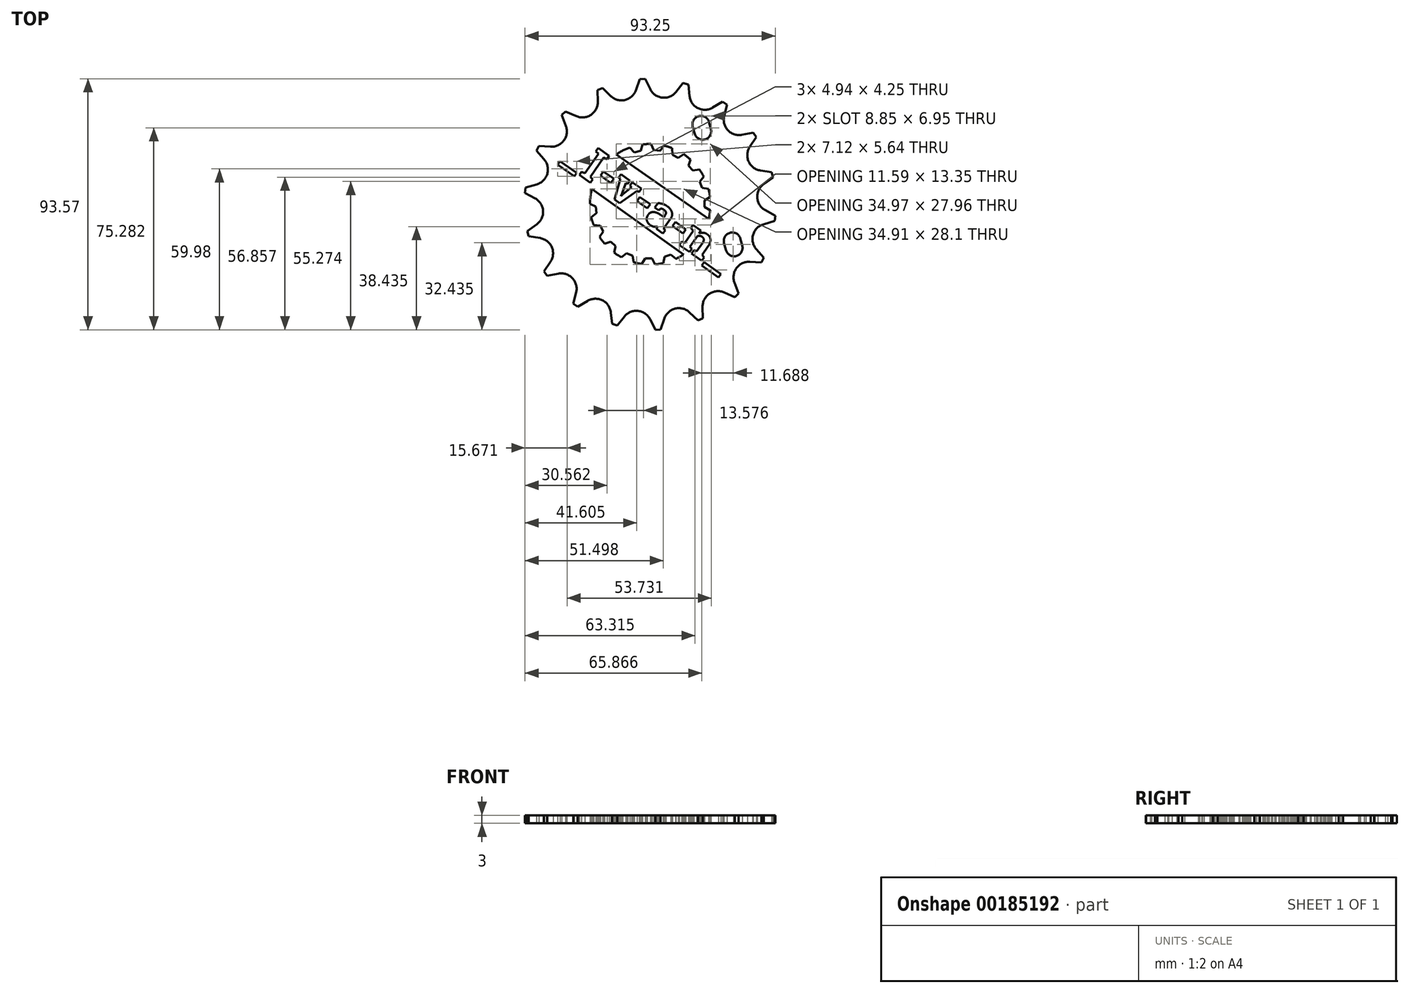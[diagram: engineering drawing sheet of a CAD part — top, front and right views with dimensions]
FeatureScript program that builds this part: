
annotation { "Feature Type Name" : "Feature", "Feature Type Description" : "" }
export const myFeature = defineFeature(function(context is Context, id is Id, definition is map)
    precondition{}
    {
        {
            var Q0;
            Q0=qCreatedBy(makeId("Top.planeOp"),FACE);
            var sketch = newSketch(context, id + "F0", { "sketchPlane" : qUnion([Q0])});
            skText(sketch, "E0", { "text": "_I-v-a-n_", "fontName": "RobotoSlab-Bold.ttf"});
            skCircle(sketch, "E1", {"center": v(-42.84, 44.1) * mm, "radius": 40 * mm});
            skLineSegment(sketch, "E2", {"start": v(-49.19, 83.6) * mm, "end": v(-46.73, 90.76) * mm, "construction": true});
            skLineSegment(sketch, "E3", {"start": v(-46.73, 90.76) * mm, "end": v(-44.73, 90.89) * mm});
            skLineSegment(sketch, "E4", {"start": v(-44.73, 90.89) * mm, "end": v(-41.4, 84.08) * mm, "construction": true});
            skLineSegment(sketch, "E5", {"start": v(-41.4, 84.08) * mm, "end": v(-49.19, 83.6) * mm, "construction": true});
            skArc(sketch, "E6", {"start": v(-42.85, 87.03) * mm, "mid": v(-38.34, 83.85) * mm, "end": v(-33.23, 85.94) * mm});
            skLineSegment(sketch, "E7", {"start": v(-42.85, 87.03) * mm, "end": v(-44.73, 90.89) * mm});
            skLineSegment(sketch, "E8", {"start": v(-48.12, 86.7) * mm, "end": v(-46.73, 90.76) * mm});
            skLineSegment(sketch, "E9.1.0", {"start": v(-55.16, 82.16) * mm, "end": v(-62.31, 79.04) * mm, "construction": true});
            skLineSegment(sketch, "E9.1.2", {"start": v(-62.31, 79.04) * mm, "end": v(-62.45, 86.62) * mm, "construction": true});
            skArc(sketch, "E9.1.3", {"start": v(-57.53, 84.44) * mm, "mid": v(-52.2, 83) * mm, "end": v(-48.12, 86.7) * mm});
            skLineSegment(sketch, "E9.1.4", {"start": v(-60.62, 87.42) * mm, "end": v(-55.16, 82.16) * mm, "construction": true});
            skLineSegment(sketch, "E9.1.5", {"start": v(-62.37, 82.33) * mm, "end": v(-62.45, 86.62) * mm});
            skLineSegment(sketch, "E9.1.6", {"start": v(-57.53, 84.44) * mm, "end": v(-60.62, 87.42) * mm});
            skLineSegment(sketch, "E9.1.7", {"start": v(-62.45, 86.62) * mm, "end": v(-60.62, 87.42) * mm});
            skLineSegment(sketch, "E9.2.0", {"start": v(-67.43, 75.65) * mm, "end": v(-73.09, 70.27) * mm, "construction": true});
            skLineSegment(sketch, "E9.2.2", {"start": v(-73.09, 70.27) * mm, "end": v(-75.8, 77.34) * mm, "construction": true});
            skArc(sketch, "E9.2.3", {"start": v(-70.44, 76.98) * mm, "mid": v(-64.94, 77.44) * mm, "end": v(-62.37, 82.33) * mm});
            skLineSegment(sketch, "E9.2.4", {"start": v(-74.36, 78.72) * mm, "end": v(-67.43, 75.65) * mm, "construction": true});
            skLineSegment(sketch, "E9.2.5", {"start": v(-74.27, 73.34) * mm, "end": v(-75.8, 77.34) * mm});
            skLineSegment(sketch, "E9.2.6", {"start": v(-70.44, 76.98) * mm, "end": v(-74.36, 78.72) * mm});
            skLineSegment(sketch, "E9.2.7", {"start": v(-75.8, 77.34) * mm, "end": v(-74.36, 78.72) * mm});
            skLineSegment(sketch, "E9.3.0", {"start": v(-76.74, 65.33) * mm, "end": v(-80.21, 58.35) * mm, "construction": true});
            skLineSegment(sketch, "E9.3.2", {"start": v(-80.21, 58.35) * mm, "end": v(-85.19, 64.06) * mm, "construction": true});
            skArc(sketch, "E9.3.3", {"start": v(-80.02, 65.56) * mm, "mid": v(-75, 67.87) * mm, "end": v(-74.27, 73.34) * mm});
            skLineSegment(sketch, "E9.3.4", {"start": v(-84.3, 65.85) * mm, "end": v(-76.74, 65.33) * mm, "construction": true});
            skLineSegment(sketch, "E9.3.5", {"start": v(-82.37, 60.83) * mm, "end": v(-85.19, 64.06) * mm});
            skLineSegment(sketch, "E9.3.6", {"start": v(-80.02, 65.56) * mm, "end": v(-84.3, 65.85) * mm});
            skLineSegment(sketch, "E9.3.7", {"start": v(-85.19, 64.06) * mm, "end": v(-84.3, 65.85) * mm});
            skLineSegment(sketch, "E9.4.0", {"start": v(-81.95, 52.45) * mm, "end": v(-82.83, 44.7) * mm, "construction": true});
            skLineSegment(sketch, "E9.4.2", {"start": v(-82.83, 44.7) * mm, "end": v(-89.46, 48.37) * mm, "construction": true});
            skArc(sketch, "E9.4.3", {"start": v(-85.11, 51.55) * mm, "mid": v(-81.2, 55.43) * mm, "end": v(-82.37, 60.83) * mm});
            skLineSegment(sketch, "E9.4.4", {"start": v(-89.24, 50.36) * mm, "end": v(-81.95, 52.45) * mm, "construction": true});
            skLineSegment(sketch, "E9.4.5", {"start": v(-85.7, 46.3) * mm, "end": v(-89.46, 48.37) * mm});
            skLineSegment(sketch, "E9.4.6", {"start": v(-85.11, 51.55) * mm, "end": v(-89.24, 50.36) * mm});
            skLineSegment(sketch, "E9.4.7", {"start": v(-89.46, 48.37) * mm, "end": v(-89.24, 50.36) * mm});
            skLineSegment(sketch, "E9.5.0", {"start": v(-82.45, 38.57) * mm, "end": v(-80.62, 30.99) * mm, "construction": true});
            skLineSegment(sketch, "E9.5.2", {"start": v(-80.62, 30.99) * mm, "end": v(-88.1, 32.17) * mm, "construction": true});
            skArc(sketch, "E9.5.3", {"start": v(-85.1, 36.64) * mm, "mid": v(-82.76, 41.63) * mm, "end": v(-85.7, 46.3) * mm});
            skLineSegment(sketch, "E9.5.4", {"start": v(-88.58, 34.11) * mm, "end": v(-82.45, 38.57) * mm, "construction": true});
            skLineSegment(sketch, "E9.5.5", {"start": v(-83.87, 31.5) * mm, "end": v(-88.1, 32.17) * mm});
            skLineSegment(sketch, "E9.5.6", {"start": v(-85.1, 36.64) * mm, "end": v(-88.58, 34.11) * mm});
            skLineSegment(sketch, "E9.5.7", {"start": v(-88.1, 32.17) * mm, "end": v(-88.58, 34.11) * mm});
            skLineSegment(sketch, "E9.6.0", {"start": v(-78.17, 25.36) * mm, "end": v(-73.86, 18.86) * mm, "construction": true});
            skLineSegment(sketch, "E9.6.2", {"start": v(-73.86, 18.86) * mm, "end": v(-81.3, 17.4) * mm, "construction": true});
            skArc(sketch, "E9.6.3", {"start": v(-80, 22.63) * mm, "mid": v(-79.5, 28.13) * mm, "end": v(-83.87, 31.5) * mm});
            skLineSegment(sketch, "E9.6.4", {"start": v(-82.4, 19.07) * mm, "end": v(-78.17, 25.36) * mm, "construction": true});
            skLineSegment(sketch, "E9.6.5", {"start": v(-77.09, 18.23) * mm, "end": v(-81.3, 17.4) * mm});
            skLineSegment(sketch, "E9.6.6", {"start": v(-80, 22.63) * mm, "end": v(-82.4, 19.07) * mm});
            skLineSegment(sketch, "E9.6.7", {"start": v(-81.3, 17.4) * mm, "end": v(-82.4, 19.07) * mm});
            skLineSegment(sketch, "E9.7.0", {"start": v(-69.63, 14.4) * mm, "end": v(-63.35, 9.77) * mm, "construction": true});
            skLineSegment(sketch, "E9.7.2", {"start": v(-63.35, 9.77) * mm, "end": v(-69.85, 5.86) * mm, "construction": true});
            skArc(sketch, "E9.7.3", {"start": v(-70.42, 11.21) * mm, "mid": v(-71.83, 16.55) * mm, "end": v(-77.09, 18.23) * mm});
            skLineSegment(sketch, "E9.7.4", {"start": v(-71.45, 7.05) * mm, "end": v(-69.63, 14.4) * mm, "construction": true});
            skLineSegment(sketch, "E9.7.5", {"start": v(-66.17, 8.07) * mm, "end": v(-69.85, 5.86) * mm});
            skLineSegment(sketch, "E9.7.6", {"start": v(-70.42, 11.21) * mm, "end": v(-71.45, 7.05) * mm});
            skLineSegment(sketch, "E9.7.7", {"start": v(-69.85, 5.86) * mm, "end": v(-71.45, 7.05) * mm});
            skLineSegment(sketch, "E9.8.0", {"start": v(-57.85, 7.03) * mm, "end": v(-50.37, 4.82) * mm, "construction": true});
            skLineSegment(sketch, "E9.8.2", {"start": v(-50.37, 4.82) * mm, "end": v(-55.14, -1.07) * mm, "construction": true});
            skArc(sketch, "E9.8.3", {"start": v(-57.5, 3.76) * mm, "mid": v(-60.66, 8.3) * mm, "end": v(-66.17, 8.07) * mm});
            skLineSegment(sketch, "E9.8.4", {"start": v(-57.05, -0.5) * mm, "end": v(-57.85, 7.03) * mm, "construction": true});
            skLineSegment(sketch, "E9.8.5", {"start": v(-52.44, 2.26) * mm, "end": v(-55.14, -1.07) * mm});
            skLineSegment(sketch, "E9.8.6", {"start": v(-57.5, 3.76) * mm, "end": v(-57.05, -0.5) * mm});
            skLineSegment(sketch, "E9.8.7", {"start": v(-55.14, -1.07) * mm, "end": v(-57.05, -0.5) * mm});
            skLineSegment(sketch, "E9.9.0", {"start": v(-44.27, 4.13) * mm, "end": v(-36.48, 4.61) * mm, "construction": true});
            skLineSegment(sketch, "E9.9.2", {"start": v(-36.48, 4.61) * mm, "end": v(-38.94, -2.55) * mm, "construction": true});
            skArc(sketch, "E9.9.3", {"start": v(-42.82, 1.18) * mm, "mid": v(-47.33, 4.36) * mm, "end": v(-52.44, 2.26) * mm});
            skLineSegment(sketch, "E9.9.4", {"start": v(-40.94, -2.68) * mm, "end": v(-44.27, 4.13) * mm, "construction": true});
            skLineSegment(sketch, "E9.9.5", {"start": v(-37.55, 1.5) * mm, "end": v(-38.94, -2.55) * mm});
            skLineSegment(sketch, "E9.9.6", {"start": v(-42.82, 1.18) * mm, "end": v(-40.94, -2.68) * mm});
            skLineSegment(sketch, "E9.9.7", {"start": v(-38.94, -2.55) * mm, "end": v(-40.94, -2.68) * mm});
            skLineSegment(sketch, "E9.10.0", {"start": v(-30.5, 6.05) * mm, "end": v(-23.36, 9.17) * mm, "construction": true});
            skLineSegment(sketch, "E9.10.2", {"start": v(-23.36, 9.17) * mm, "end": v(-23.22, 1.6) * mm, "construction": true});
            skArc(sketch, "E9.10.3", {"start": v(-28.14, 3.77) * mm, "mid": v(-33.47, 5.22) * mm, "end": v(-37.55, 1.5) * mm});
            skLineSegment(sketch, "E9.10.4", {"start": v(-25.05, 0.8) * mm, "end": v(-30.5, 6.05) * mm, "construction": true});
            skLineSegment(sketch, "E9.10.5", {"start": v(-23.3, 5.88) * mm, "end": v(-23.22, 1.6) * mm});
            skLineSegment(sketch, "E9.10.6", {"start": v(-28.14, 3.77) * mm, "end": v(-25.05, 0.8) * mm});
            skLineSegment(sketch, "E9.10.7", {"start": v(-23.22, 1.6) * mm, "end": v(-25.05, 0.8) * mm});
            skLineSegment(sketch, "E9.11.0", {"start": v(-18.24, 12.56) * mm, "end": v(-12.58, 17.93) * mm, "construction": true});
            skLineSegment(sketch, "E9.11.2", {"start": v(-12.58, 17.93) * mm, "end": v(-9.86, 10.86) * mm, "construction": true});
            skArc(sketch, "E9.11.3", {"start": v(-15.23, 11.23) * mm, "mid": v(-20.73, 10.77) * mm, "end": v(-23.3, 5.88) * mm});
            skLineSegment(sketch, "E9.11.4", {"start": v(-11.31, 9.49) * mm, "end": v(-18.24, 12.56) * mm, "construction": true});
            skLineSegment(sketch, "E9.11.5", {"start": v(-11.4, 14.87) * mm, "end": v(-9.86, 10.86) * mm});
            skLineSegment(sketch, "E9.11.6", {"start": v(-15.23, 11.23) * mm, "end": v(-11.31, 9.49) * mm});
            skLineSegment(sketch, "E9.11.7", {"start": v(-9.86, 10.86) * mm, "end": v(-11.31, 9.49) * mm});
            skLineSegment(sketch, "E9.12.0", {"start": v(-8.93, 22.88) * mm, "end": v(-5.46, 29.86) * mm, "construction": true});
            skLineSegment(sketch, "E9.12.2", {"start": v(-5.46, 29.86) * mm, "end": v(-0.48, 24.15) * mm, "construction": true});
            skArc(sketch, "E9.12.3", {"start": v(-5.65, 22.65) * mm, "mid": v(-10.66, 20.34) * mm, "end": v(-11.4, 14.87) * mm});
            skLineSegment(sketch, "E9.12.4", {"start": v(-1.37, 22.35) * mm, "end": v(-8.93, 22.88) * mm, "construction": true});
            skLineSegment(sketch, "E9.12.5", {"start": v(-3.3, 27.38) * mm, "end": v(-0.48, 24.15) * mm});
            skLineSegment(sketch, "E9.12.6", {"start": v(-5.65, 22.65) * mm, "end": v(-1.37, 22.35) * mm});
            skLineSegment(sketch, "E9.12.7", {"start": v(-0.48, 24.15) * mm, "end": v(-1.37, 22.35) * mm});
            skLineSegment(sketch, "E9.13.0", {"start": v(-3.72, 35.75) * mm, "end": v(-2.84, 43.5) * mm, "construction": true});
            skLineSegment(sketch, "E9.13.2", {"start": v(-2.84, 43.5) * mm, "end": v(3.79, 39.83) * mm, "construction": true});
            skArc(sketch, "E9.13.3", {"start": v(-0.56, 36.66) * mm, "mid": v(-4.47, 32.77) * mm, "end": v(-3.3, 27.38) * mm});
            skLineSegment(sketch, "E9.13.4", {"start": v(3.56, 37.85) * mm, "end": v(-3.72, 35.75) * mm, "construction": true});
            skLineSegment(sketch, "E9.13.5", {"start": v(0.04, 41.91) * mm, "end": v(3.79, 39.83) * mm});
            skLineSegment(sketch, "E9.13.6", {"start": v(-0.56, 36.66) * mm, "end": v(3.56, 37.85) * mm});
            skLineSegment(sketch, "E9.13.7", {"start": v(3.79, 39.83) * mm, "end": v(3.56, 37.85) * mm});
            skLineSegment(sketch, "E9.14.0", {"start": v(-3.22, 49.64) * mm, "end": v(-5.05, 57.22) * mm, "construction": true});
            skLineSegment(sketch, "E9.14.2", {"start": v(-5.05, 57.22) * mm, "end": v(2.44, 56.04) * mm, "construction": true});
            skArc(sketch, "E9.14.3", {"start": v(-0.56, 51.57) * mm, "mid": v(-2.91, 46.58) * mm, "end": v(0.04, 41.91) * mm});
            skLineSegment(sketch, "E9.14.4", {"start": v(2.9, 54.1) * mm, "end": v(-3.22, 49.64) * mm, "construction": true});
            skLineSegment(sketch, "E9.14.5", {"start": v(-1.8, 56.7) * mm, "end": v(2.44, 56.04) * mm});
            skLineSegment(sketch, "E9.14.6", {"start": v(-0.56, 51.57) * mm, "end": v(2.9, 54.1) * mm});
            skLineSegment(sketch, "E9.14.7", {"start": v(2.44, 56.04) * mm, "end": v(2.9, 54.1) * mm});
            skLineSegment(sketch, "E9.15.0", {"start": v(-7.5, 62.85) * mm, "end": v(-11.81, 69.35) * mm, "construction": true});
            skLineSegment(sketch, "E9.15.2", {"start": v(-11.81, 69.35) * mm, "end": v(-4.37, 70.8) * mm, "construction": true});
            skArc(sketch, "E9.15.3", {"start": v(-5.66, 65.58) * mm, "mid": v(-6.17, 60.08) * mm, "end": v(-1.8, 56.7) * mm});
            skLineSegment(sketch, "E9.15.4", {"start": v(-3.27, 69.14) * mm, "end": v(-7.5, 62.85) * mm, "construction": true});
            skLineSegment(sketch, "E9.15.5", {"start": v(-8.58, 69.98) * mm, "end": v(-4.37, 70.8) * mm});
            skLineSegment(sketch, "E9.15.6", {"start": v(-5.66, 65.58) * mm, "end": v(-3.27, 69.14) * mm});
            skLineSegment(sketch, "E9.15.7", {"start": v(-4.37, 70.8) * mm, "end": v(-3.27, 69.14) * mm});
            skLineSegment(sketch, "E9.16.0", {"start": v(-16.04, 73.8) * mm, "end": v(-22.32, 78.44) * mm, "construction": true});
            skLineSegment(sketch, "E9.16.2", {"start": v(-22.32, 78.44) * mm, "end": v(-15.83, 82.35) * mm, "construction": true});
            skArc(sketch, "E9.16.3", {"start": v(-15.25, 77) * mm, "mid": v(-13.84, 71.66) * mm, "end": v(-8.58, 69.98) * mm});
            skLineSegment(sketch, "E9.16.4", {"start": v(-14.22, 81.16) * mm, "end": v(-16.04, 73.8) * mm, "construction": true});
            skLineSegment(sketch, "E9.16.5", {"start": v(-19.5, 80.14) * mm, "end": v(-15.83, 82.35) * mm});
            skLineSegment(sketch, "E9.16.6", {"start": v(-15.25, 77) * mm, "end": v(-14.22, 81.16) * mm});
            skLineSegment(sketch, "E9.16.7", {"start": v(-15.83, 82.35) * mm, "end": v(-14.22, 81.16) * mm});
            skLineSegment(sketch, "E9.17.0", {"start": v(-27.82, 81.18) * mm, "end": v(-35.3, 83.39) * mm, "construction": true});
            skLineSegment(sketch, "E9.17.2", {"start": v(-35.3, 83.39) * mm, "end": v(-30.53, 89.28) * mm, "construction": true});
            skArc(sketch, "E9.17.3", {"start": v(-28.16, 84.45) * mm, "mid": v(-25.02, 79.92) * mm, "end": v(-19.5, 80.14) * mm});
            skLineSegment(sketch, "E9.17.4", {"start": v(-28.62, 88.71) * mm, "end": v(-27.82, 81.18) * mm, "construction": true});
            skLineSegment(sketch, "E9.17.5", {"start": v(-33.23, 85.94) * mm, "end": v(-30.53, 89.28) * mm});
            skLineSegment(sketch, "E9.17.6", {"start": v(-28.16, 84.45) * mm, "end": v(-28.62, 88.71) * mm});
            skLineSegment(sketch, "E9.17.7", {"start": v(-30.53, 89.28) * mm, "end": v(-28.62, 88.71) * mm});
            skLineSegment(sketch, "E10", {"start": v(-102.27, 86.15) * mm, "end": v(16.6, 2.06) * mm, "construction": true});
            skLineSegment(sketch, "E11", {"start": v(-55.45, 62.7) * mm, "end": v(-21.04, 38.61) * mm});
            skArc(sketch, "E12", {"start": v(-55.45, 62.7) * mm, "mid": v(-29.95, 62.51) * mm, "end": v(-21.04, 38.61) * mm, "construction": true});
            skLineSegment(sketch, "E13", {"start": v(-50.46, 65.24) * mm, "end": v(-48.76, 63.46) * mm});
            skLineSegment(sketch, "E14", {"start": v(-48.76, 63.46) * mm, "end": v(-46.37, 64.04) * mm});
            skLineSegment(sketch, "E15", {"start": v(-46.37, 64.04) * mm, "end": v(-45.67, 66.4) * mm});
            skLineSegment(sketch, "E16", {"start": v(-45.67, 66.4) * mm, "end": v(-50.46, 65.24) * mm, "construction": true});
            skLineSegment(sketch, "E17", {"start": v(-53.55, 88.57) * mm, "end": v(-42.84, 44.1) * mm, "construction": true});
            skPoint(sketch, "E18", {"position": v(-47.57, 63.75) * mm});
            skLineSegment(sketch, "E19.1.0", {"start": v(-42.53, 66.57) * mm, "end": v(-41.57, 64.3) * mm});
            skLineSegment(sketch, "E19.1.1", {"start": v(-41.57, 64.3) * mm, "end": v(-39.13, 64) * mm});
            skLineSegment(sketch, "E19.1.2", {"start": v(-39.13, 64) * mm, "end": v(-37.65, 65.97) * mm});
            skLineSegment(sketch, "E19.2.0", {"start": v(-34.65, 65.03) * mm, "end": v(-34.55, 62.57) * mm});
            skLineSegment(sketch, "E19.2.1", {"start": v(-34.55, 62.57) * mm, "end": v(-32.37, 61.43) * mm});
            skLineSegment(sketch, "E19.2.2", {"start": v(-32.37, 61.43) * mm, "end": v(-30.29, 62.75) * mm});
            skLineSegment(sketch, "E19.3.0", {"start": v(-27.8, 60.81) * mm, "end": v(-28.58, 58.48) * mm});
            skLineSegment(sketch, "E19.3.1", {"start": v(-28.58, 58.48) * mm, "end": v(-26.94, 56.64) * mm});
            skLineSegment(sketch, "E19.3.2", {"start": v(-26.94, 56.64) * mm, "end": v(-24.53, 57.14) * mm});
            skLineSegment(sketch, "E19.4.0", {"start": v(-22.89, 54.46) * mm, "end": v(-24.43, 52.54) * mm});
            skLineSegment(sketch, "E19.4.1", {"start": v(-24.43, 52.54) * mm, "end": v(-23.55, 50.25) * mm});
            skLineSegment(sketch, "E19.4.2", {"start": v(-23.55, 50.25) * mm, "end": v(-21.11, 49.87) * mm});
            skLineSegment(sketch, "E19.5.0", {"start": v(-20.52, 46.78) * mm, "end": v(-22.64, 45.53) * mm});
            skLineSegment(sketch, "E19.5.1", {"start": v(-22.64, 45.53) * mm, "end": v(-22.62, 43.07) * mm});
            skLineSegment(sketch, "E19.5.2", {"start": v(-22.62, 43.07) * mm, "end": v(-20.48, 41.86) * mm});
            skLineSegment(sketch, "E19.anchor1", {"start": v(-42.84, 44.1) * mm, "end": v(-48.76, 63.46) * mm, "construction": true});
            skLineSegment(sketch, "E19.anchor2", {"start": v(-42.84, 44.1) * mm, "end": v(-22.64, 45.53) * mm, "construction": true});
            skArc(sketch, "E20", {"start": v(-55.45, 62.7) * mm, "mid": v(-53.03, 64.13) * mm, "end": v(-50.46, 65.24) * mm});
            skArc(sketch, "E21", {"start": v(-45.67, 66.4) * mm, "mid": v(-44.1, 66.54) * mm, "end": v(-42.53, 66.57) * mm});
            skArc(sketch, "E22", {"start": v(-37.65, 65.97) * mm, "mid": v(-36.13, 65.55) * mm, "end": v(-34.65, 65.03) * mm});
            skArc(sketch, "E23", {"start": v(-30.29, 62.75) * mm, "mid": v(-29.01, 61.82) * mm, "end": v(-27.8, 60.81) * mm});
            skArc(sketch, "E24", {"start": v(-24.53, 57.14) * mm, "mid": v(-23.66, 55.83) * mm, "end": v(-22.89, 54.46) * mm});
            skArc(sketch, "E25", {"start": v(-21.11, 49.87) * mm, "mid": v(-20.76, 48.33) * mm, "end": v(-20.52, 46.78) * mm});
            skArc(sketch, "E26", {"start": v(-20.48, 41.86) * mm, "mid": v(-20.7, 40.22) * mm, "end": v(-21.04, 38.61) * mm});
            skLineSegment(sketch, "E27.MirrorCS", {"start": v(-63.06, 43.25) * mm, "end": v(-62.8, 40.8) * mm});
            skArc(sketch, "E28.MirrorCS", {"start": v(-64.57, 49.8) * mm, "mid": v(-65.11, 47.05) * mm, "end": v(-65.3, 44.25) * mm});
            skLineSegment(sketch, "E29.MirrorCS", {"start": v(-59.84, 29.42) * mm, "end": v(-57.5, 30.14) * mm});
            skLineSegment(sketch, "E30.MirrorCS", {"start": v(-62.8, 40.8) * mm, "end": v(-64.8, 39.36) * mm});
            skLineSegment(sketch, "E31.MirrorCS", {"start": v(-37.45, 24.59) * mm, "end": v(-35.13, 25.39) * mm});
            skLineSegment(sketch, "E32.MirrorCS", {"start": v(-53.59, 24.37) * mm, "end": v(-51.64, 25.88) * mm});
            skLineSegment(sketch, "E33.MirrorCS", {"start": v(-37.93, 22.17) * mm, "end": v(-37.45, 24.59) * mm});
            skLineSegment(sketch, "E34.MirrorCS", {"start": v(-63.92, 36.34) * mm, "end": v(-61.47, 36.19) * mm});
            skLineSegment(sketch, "E35.MirrorCS", {"start": v(-42.2, 23.87) * mm, "end": v(-41.04, 21.7) * mm});
            skLineSegment(sketch, "E36.MirrorCS", {"start": v(-65.3, 44.25) * mm, "end": v(-63.06, 43.25) * mm});
            skArc(sketch, "E37.MirrorCS", {"start": v(-56.24, 26.07) * mm, "mid": v(-54.94, 25.17) * mm, "end": v(-53.59, 24.37) * mm});
            skArc(sketch, "E38.MirrorCS", {"start": v(-64.57, 49.8) * mm, "mid": v(-55.9, 25.82) * mm, "end": v(-30.4, 25.38) * mm, "construction": true});
            skLineSegment(sketch, "E39.MirrorCS", {"start": v(-44.66, 23.94) * mm, "end": v(-42.2, 23.87) * mm});
            skArc(sketch, "E40.MirrorCS", {"start": v(-64.8, 39.36) * mm, "mid": v(-64.42, 37.83) * mm, "end": v(-63.92, 36.34) * mm});
            skLineSegment(sketch, "E41.MirrorCS", {"start": v(-45.96, 21.85) * mm, "end": v(-44.66, 23.94) * mm});
            skLineSegment(sketch, "E42.MirrorCS", {"start": v(-64.57, 49.8) * mm, "end": v(-30.4, 25.38) * mm});
            skLineSegment(sketch, "E43.MirrorCS", {"start": v(-49.36, 24.94) * mm, "end": v(-49.03, 22.5) * mm});
            skLineSegment(sketch, "E44.MirrorCS", {"start": v(-61.47, 36.19) * mm, "end": v(-60.37, 33.99) * mm});
            skArc(sketch, "E45.MirrorCS", {"start": v(-33.27, 23.77) * mm, "mid": v(-31.8, 24.52) * mm, "end": v(-30.4, 25.38) * mm});
            skLineSegment(sketch, "E46.MirrorCS", {"start": v(-51.64, 25.88) * mm, "end": v(-49.36, 24.94) * mm});
            skArc(sketch, "E47.MirrorCS", {"start": v(-41.04, 21.7) * mm, "mid": v(-39.47, 21.88) * mm, "end": v(-37.93, 22.17) * mm});
            skArc(sketch, "E48.MirrorCS", {"start": v(-49.03, 22.5) * mm, "mid": v(-47.5, 22.12) * mm, "end": v(-45.96, 21.85) * mm});
            skLineSegment(sketch, "E49.MirrorCS", {"start": v(-64.8, 39.36) * mm, "end": v(-65.3, 44.25) * mm, "construction": true});
            skLineSegment(sketch, "E50.MirrorCS", {"start": v(-57.5, 30.14) * mm, "end": v(-55.69, 28.46) * mm});
            skLineSegment(sketch, "E51.MirrorCS", {"start": v(-60.37, 33.99) * mm, "end": v(-61.73, 31.93) * mm});
            skPoint(sketch, "E52.MirrorP", {"position": v(-62.93, 42.03) * mm});
            skArc(sketch, "E53.MirrorCS", {"start": v(-61.73, 31.93) * mm, "mid": v(-60.83, 30.64) * mm, "end": v(-59.84, 29.42) * mm});
            skLineSegment(sketch, "E54.MirrorCS", {"start": v(-35.13, 25.39) * mm, "end": v(-33.27, 23.77) * mm});
            skLineSegment(sketch, "E55.MirrorCS", {"start": v(-55.69, 28.46) * mm, "end": v(-56.24, 26.07) * mm});
            const initialGuessF0  = {"E0": [-0.07709, 0.06056, 0.81915, -0.57358, 0.01233]};
            skSetInitialGuess(sketch, initialGuessF0);
            skSolve(sketch);
        }
        {
            var Q0;
            Q0 = qSketchRegion(id + "F0", true);
            extrude(context, id + "F1", {"entities" : qUnion([Q0]), "flatOperationType" : FlatOperationType.REMOVE, "offsetDistance" : 25 * mm, "depth" : 3 * mm, "domain" : OperationDomain.MODEL});
        }
        {
            var Q0;
            Q0=makeQuery(id+"F1.opExtrude","CAP_FACE",FACE,{"disambiguationData":[OSD([sQuery(id+"F0.wireOp",EDGE,"E0.sketch_text.stroke-0"),sQuery(id+"F0.wireOp",EDGE,"E0.sketch_text.stroke-1"),sQuery(id+"F0.wireOp",EDGE,"E0.sketch_text.stroke-2"),sQuery(id+"F0.wireOp",EDGE,"E0.sketch_text.stroke-3"),sQuery(id+"F0.wireOp",EDGE,"E0.sketch_text.stroke-4"),sQuery(id+"F0.wireOp",EDGE,"E0.sketch_text.stroke-5"),sQuery(id+"F0.wireOp",EDGE,"E0.sketch_text.stroke-6"),sQuery(id+"F0.wireOp",EDGE,"E0.sketch_text.stroke-7"),sQuery(id+"F0.wireOp",EDGE,"E0.sketch_text.stroke-8"),sQuery(id+"F0.wireOp",EDGE,"E0.sketch_text.stroke-9"),sQuery(id+"F0.wireOp",EDGE,"E0.sketch_text.stroke-10"),sQuery(id+"F0.wireOp",EDGE,"E0.sketch_text.stroke-11"),sQuery(id+"F0.wireOp",EDGE,"E0.sketch_text.stroke-12"),sQuery(id+"F0.wireOp",EDGE,"E0.sketch_text.stroke-13"),sQuery(id+"F0.wireOp",EDGE,"E0.sketch_text.stroke-14"),sQuery(id+"F0.wireOp",EDGE,"E0.sketch_text.stroke-15"),sQuery(id+"F0.wireOp",EDGE,"E0.sketch_text.stroke-16"),sQuery(id+"F0.wireOp",EDGE,"E0.sketch_text.stroke-17"),sQuery(id+"F0.wireOp",EDGE,"E0.sketch_text.stroke-18"),sQuery(id+"F0.wireOp",EDGE,"E0.sketch_text.stroke-19"),sQuery(id+"F0.wireOp",EDGE,"E0.sketch_text.stroke-20"),sQuery(id+"F0.wireOp",EDGE,"E0.sketch_text.stroke-21"),sQuery(id+"F0.wireOp",EDGE,"E0.sketch_text.stroke-22"),sQuery(id+"F0.wireOp",EDGE,"E0.sketch_text.stroke-23"),sQuery(id+"F0.wireOp",EDGE,"E0.sketch_text.stroke-24"),sQuery(id+"F0.wireOp",EDGE,"E0.sketch_text.stroke-25"),sQuery(id+"F0.wireOp",EDGE,"E0.sketch_text.stroke-26"),sQuery(id+"F0.wireOp",EDGE,"E0.sketch_text.stroke-27"),sQuery(id+"F0.wireOp",EDGE,"E0.sketch_text.stroke-28"),sQuery(id+"F0.wireOp",EDGE,"E0.sketch_text.stroke-29"),sQuery(id+"F0.wireOp",EDGE,"E0.sketch_text.stroke-30"),sQuery(id+"F0.wireOp",EDGE,"E0.sketch_text.stroke-31"),sQuery(id+"F0.wireOp",EDGE,"E0.sketch_text.stroke-32"),sQuery(id+"F0.wireOp",EDGE,"E0.sketch_text.stroke-33"),sQuery(id+"F0.wireOp",EDGE,"E0.sketch_text.stroke-34"),sQuery(id+"F0.wireOp",EDGE,"E0.sketch_text.stroke-35"),sQuery(id+"F0.wireOp",EDGE,"E0.sketch_text.stroke-36"),sQuery(id+"F0.wireOp",EDGE,"E0.sketch_text.stroke-37"),sQuery(id+"F0.wireOp",EDGE,"E0.sketch_text.stroke-38"),sQuery(id+"F0.wireOp",EDGE,"E0.sketch_text.stroke-39"),sQuery(id+"F0.wireOp",EDGE,"E0.sketch_text.stroke-40"),sQuery(id+"F0.wireOp",EDGE,"E0.sketch_text.stroke-41"),sQuery(id+"F0.wireOp",EDGE,"E0.sketch_text.stroke-42"),sQuery(id+"F0.wireOp",EDGE,"E0.sketch_text.stroke-43"),sQuery(id+"F0.wireOp",EDGE,"E0.sketch_text.stroke-44"),sQuery(id+"F0.wireOp",EDGE,"E0.sketch_text.stroke-45"),sQuery(id+"F0.wireOp",EDGE,"E0.sketch_text.stroke-46"),sQuery(id+"F0.wireOp",EDGE,"E0.sketch_text.stroke-47"),sQuery(id+"F0.wireOp",EDGE,"E0.sketch_text.stroke-48"),sQuery(id+"F0.wireOp",EDGE,"E0.sketch_text.stroke-49"),sQuery(id+"F0.wireOp",EDGE,"E0.sketch_text.stroke-50"),sQuery(id+"F0.wireOp",EDGE,"E0.sketch_text.stroke-51"),sQuery(id+"F0.wireOp",EDGE,"E0.sketch_text.stroke-52"),sQuery(id+"F0.wireOp",EDGE,"E0.sketch_text.stroke-53"),sQuery(id+"F0.wireOp",EDGE,"E0.sketch_text.stroke-54"),sQuery(id+"F0.wireOp",EDGE,"E0.sketch_text.stroke-55"),sQuery(id+"F0.wireOp",EDGE,"E0.sketch_text.stroke-56"),sQuery(id+"F0.wireOp",EDGE,"E0.sketch_text.stroke-57"),sQuery(id+"F0.wireOp",EDGE,"E0.sketch_text.stroke-58"),sQuery(id+"F0.wireOp",EDGE,"E0.sketch_text.stroke-59"),sQuery(id+"F0.wireOp",EDGE,"E0.sketch_text.stroke-60"),sQuery(id+"F0.wireOp",EDGE,"E0.sketch_text.stroke-61"),sQuery(id+"F0.wireOp",EDGE,"E0.sketch_text.stroke-62"),sQuery(id+"F0.wireOp",EDGE,"E0.sketch_text.stroke-63"),sQuery(id+"F0.wireOp",EDGE,"E0.sketch_text.stroke-64"),sQuery(id+"F0.wireOp",EDGE,"E0.sketch_text.stroke-65"),sQuery(id+"F0.wireOp",EDGE,"E0.sketch_text.stroke-66"),sQuery(id+"F0.wireOp",EDGE,"E0.sketch_text.stroke-67"),sQuery(id+"F0.wireOp",EDGE,"E0.sketch_text.stroke-68"),sQuery(id+"F0.wireOp",EDGE,"E0.sketch_text.stroke-77"),sQuery(id+"F0.wireOp",EDGE,"E0.sketch_text.stroke-78"),sQuery(id+"F0.wireOp",EDGE,"E0.sketch_text.stroke-79"),sQuery(id+"F0.wireOp",EDGE,"E0.sketch_text.stroke-80"),sQuery(id+"F0.wireOp",EDGE,"E0.sketch_text.stroke-81"),sQuery(id+"F0.wireOp",EDGE,"E0.sketch_text.stroke-82"),sQuery(id+"F0.wireOp",EDGE,"E0.sketch_text.stroke-83"),sQuery(id+"F0.wireOp",EDGE,"E0.sketch_text.stroke-84"),sQuery(id+"F0.wireOp",EDGE,"E0.sketch_text.stroke-85"),sQuery(id+"F0.wireOp",EDGE,"E0.sketch_text.stroke-86"),sQuery(id+"F0.wireOp",EDGE,"E0.sketch_text.stroke-87"),sQuery(id+"F0.wireOp",EDGE,"E0.sketch_text.stroke-88"),sQuery(id+"F0.wireOp",EDGE,"E0.sketch_text.stroke-89"),sQuery(id+"F0.wireOp",EDGE,"E0.sketch_text.stroke-90"),sQuery(id+"F0.wireOp",EDGE,"E0.sketch_text.stroke-91"),sQuery(id+"F0.wireOp",EDGE,"E0.sketch_text.stroke-92"),sQuery(id+"F0.wireOp",EDGE,"E0.sketch_text.stroke-93"),sQuery(id+"F0.wireOp",EDGE,"E0.sketch_text.stroke-94"),sQuery(id+"F0.wireOp",EDGE,"E0.sketch_text.stroke-95"),sQuery(id+"F0.wireOp",EDGE,"E0.sketch_text.stroke-96"),sQuery(id+"F0.wireOp",EDGE,"E0.sketch_text.stroke-97"),sQuery(id+"F0.wireOp",EDGE,"E0.sketch_text.stroke-98"),sQuery(id+"F0.wireOp",EDGE,"E0.sketch_text.stroke-99"),sQuery(id+"F0.wireOp",EDGE,"E0.sketch_text.stroke-100"),sQuery(id+"F0.wireOp",EDGE,"E0.sketch_text.stroke-101"),sQuery(id+"F0.wireOp",EDGE,"E0.sketch_text.stroke-102"),sQuery(id+"F0.wireOp",EDGE,"E0.sketch_text.stroke-103"),sQuery(id+"F0.wireOp",EDGE,"E0.sketch_text.stroke-104"),sQuery(id+"F0.wireOp",EDGE,"E0.sketch_text.stroke-105"),sQuery(id+"F0.wireOp",EDGE,"E0.sketch_text.stroke-106"),sQuery(id+"F0.wireOp",EDGE,"E0.sketch_text.stroke-107"),sQuery(id+"F0.wireOp",EDGE,"E0.sketch_text.stroke-108"),sQuery(id+"F0.wireOp",EDGE,"E0.sketch_text.stroke-109"),sQuery(id+"F0.wireOp",EDGE,"E0.sketch_text.stroke-110"),sQuery(id+"F0.wireOp",EDGE,"E3"),sQuery(id+"F0.wireOp",EDGE,"E6"),sQuery(id+"F0.wireOp",EDGE,"E7"),sQuery(id+"F0.wireOp",EDGE,"E8"),sQuery(id+"F0.wireOp",EDGE,"E9.1.3"),sQuery(id+"F0.wireOp",EDGE,"E9.1.5"),sQuery(id+"F0.wireOp",EDGE,"E9.1.6"),sQuery(id+"F0.wireOp",EDGE,"E9.1.7"),sQuery(id+"F0.wireOp",EDGE,"E9.2.3"),sQuery(id+"F0.wireOp",EDGE,"E9.2.5"),sQuery(id+"F0.wireOp",EDGE,"E9.2.6"),sQuery(id+"F0.wireOp",EDGE,"E9.2.7"),sQuery(id+"F0.wireOp",EDGE,"E9.3.3"),sQuery(id+"F0.wireOp",EDGE,"E9.3.5"),sQuery(id+"F0.wireOp",EDGE,"E9.3.6"),sQuery(id+"F0.wireOp",EDGE,"E9.3.7"),sQuery(id+"F0.wireOp",EDGE,"E9.4.3"),sQuery(id+"F0.wireOp",EDGE,"E9.4.5"),sQuery(id+"F0.wireOp",EDGE,"E9.4.6"),sQuery(id+"F0.wireOp",EDGE,"E9.4.7"),sQuery(id+"F0.wireOp",EDGE,"E9.5.3"),sQuery(id+"F0.wireOp",EDGE,"E9.5.5"),sQuery(id+"F0.wireOp",EDGE,"E9.5.6"),sQuery(id+"F0.wireOp",EDGE,"E9.5.7"),sQuery(id+"F0.wireOp",EDGE,"E9.6.3"),sQuery(id+"F0.wireOp",EDGE,"E9.6.5"),sQuery(id+"F0.wireOp",EDGE,"E9.6.6"),sQuery(id+"F0.wireOp",EDGE,"E9.6.7"),sQuery(id+"F0.wireOp",EDGE,"E9.7.3"),sQuery(id+"F0.wireOp",EDGE,"E9.7.5"),sQuery(id+"F0.wireOp",EDGE,"E9.7.6"),sQuery(id+"F0.wireOp",EDGE,"E9.7.7"),sQuery(id+"F0.wireOp",EDGE,"E9.8.3"),sQuery(id+"F0.wireOp",EDGE,"E9.8.5"),sQuery(id+"F0.wireOp",EDGE,"E9.8.6"),sQuery(id+"F0.wireOp",EDGE,"E9.8.7"),sQuery(id+"F0.wireOp",EDGE,"E9.9.3"),sQuery(id+"F0.wireOp",EDGE,"E9.9.5"),sQuery(id+"F0.wireOp",EDGE,"E9.9.6"),sQuery(id+"F0.wireOp",EDGE,"E9.9.7"),sQuery(id+"F0.wireOp",EDGE,"E9.10.3"),sQuery(id+"F0.wireOp",EDGE,"E9.10.5"),sQuery(id+"F0.wireOp",EDGE,"E9.10.6"),sQuery(id+"F0.wireOp",EDGE,"E9.10.7"),sQuery(id+"F0.wireOp",EDGE,"E9.11.3"),sQuery(id+"F0.wireOp",EDGE,"E9.11.5"),sQuery(id+"F0.wireOp",EDGE,"E9.11.6"),sQuery(id+"F0.wireOp",EDGE,"E9.11.7"),sQuery(id+"F0.wireOp",EDGE,"E9.12.3"),sQuery(id+"F0.wireOp",EDGE,"E9.12.5"),sQuery(id+"F0.wireOp",EDGE,"E9.12.6"),sQuery(id+"F0.wireOp",EDGE,"E9.12.7"),sQuery(id+"F0.wireOp",EDGE,"E9.13.3"),sQuery(id+"F0.wireOp",EDGE,"E9.13.5"),sQuery(id+"F0.wireOp",EDGE,"E9.13.6"),sQuery(id+"F0.wireOp",EDGE,"E9.13.7"),sQuery(id+"F0.wireOp",EDGE,"E9.14.3"),sQuery(id+"F0.wireOp",EDGE,"E9.14.5"),sQuery(id+"F0.wireOp",EDGE,"E9.14.6"),sQuery(id+"F0.wireOp",EDGE,"E9.14.7"),sQuery(id+"F0.wireOp",EDGE,"E9.15.3"),sQuery(id+"F0.wireOp",EDGE,"E9.15.5"),sQuery(id+"F0.wireOp",EDGE,"E9.15.6"),sQuery(id+"F0.wireOp",EDGE,"E9.15.7"),sQuery(id+"F0.wireOp",EDGE,"E9.16.3"),sQuery(id+"F0.wireOp",EDGE,"E9.16.5"),sQuery(id+"F0.wireOp",EDGE,"E9.16.6"),sQuery(id+"F0.wireOp",EDGE,"E9.16.7"),sQuery(id+"F0.wireOp",EDGE,"E9.17.3"),sQuery(id+"F0.wireOp",EDGE,"E9.17.5"),sQuery(id+"F0.wireOp",EDGE,"E9.17.6"),sQuery(id+"F0.wireOp",EDGE,"E9.17.7"),sQuery(id+"F0.wireOp",EDGE,"E11"),sQuery(id+"F0.wireOp",EDGE,"E13"),sQuery(id+"F0.wireOp",EDGE,"E14"),sQuery(id+"F0.wireOp",EDGE,"E15"),sQuery(id+"F0.wireOp",EDGE,"E19.1.0"),sQuery(id+"F0.wireOp",EDGE,"E19.1.1"),sQuery(id+"F0.wireOp",EDGE,"E19.1.2"),sQuery(id+"F0.wireOp",EDGE,"E19.2.0"),sQuery(id+"F0.wireOp",EDGE,"E19.2.1"),sQuery(id+"F0.wireOp",EDGE,"E19.2.2"),sQuery(id+"F0.wireOp",EDGE,"E19.3.0"),sQuery(id+"F0.wireOp",EDGE,"E19.3.1"),sQuery(id+"F0.wireOp",EDGE,"E19.3.2"),sQuery(id+"F0.wireOp",EDGE,"E19.4.0"),sQuery(id+"F0.wireOp",EDGE,"E19.4.1"),sQuery(id+"F0.wireOp",EDGE,"E19.4.2"),sQuery(id+"F0.wireOp",EDGE,"E19.5.0"),sQuery(id+"F0.wireOp",EDGE,"E19.5.1"),sQuery(id+"F0.wireOp",EDGE,"E19.5.2"),sQuery(id+"F0.wireOp",EDGE,"E20"),sQuery(id+"F0.wireOp",EDGE,"E21"),sQuery(id+"F0.wireOp",EDGE,"E22"),sQuery(id+"F0.wireOp",EDGE,"E23"),sQuery(id+"F0.wireOp",EDGE,"E24"),sQuery(id+"F0.wireOp",EDGE,"E25"),sQuery(id+"F0.wireOp",EDGE,"E26"),sQuery(id+"F0.wireOp",EDGE,"E27.MirrorCS"),sQuery(id+"F0.wireOp",EDGE,"E28.MirrorCS"),sQuery(id+"F0.wireOp",EDGE,"E29.MirrorCS"),sQuery(id+"F0.wireOp",EDGE,"E30.MirrorCS"),sQuery(id+"F0.wireOp",EDGE,"E31.MirrorCS"),sQuery(id+"F0.wireOp",EDGE,"E32.MirrorCS"),sQuery(id+"F0.wireOp",EDGE,"E33.MirrorCS"),sQuery(id+"F0.wireOp",EDGE,"E34.MirrorCS"),sQuery(id+"F0.wireOp",EDGE,"E35.MirrorCS"),sQuery(id+"F0.wireOp",EDGE,"E36.MirrorCS"),sQuery(id+"F0.wireOp",EDGE,"E37.MirrorCS"),sQuery(id+"F0.wireOp",EDGE,"E39.MirrorCS"),sQuery(id+"F0.wireOp",EDGE,"E40.MirrorCS"),sQuery(id+"F0.wireOp",EDGE,"E41.MirrorCS"),sQuery(id+"F0.wireOp",EDGE,"E42.MirrorCS"),sQuery(id+"F0.wireOp",EDGE,"E43.MirrorCS"),sQuery(id+"F0.wireOp",EDGE,"E44.MirrorCS"),sQuery(id+"F0.wireOp",EDGE,"E45.MirrorCS"),sQuery(id+"F0.wireOp",EDGE,"E46.MirrorCS"),sQuery(id+"F0.wireOp",EDGE,"E47.MirrorCS"),sQuery(id+"F0.wireOp",EDGE,"E48.MirrorCS"),sQuery(id+"F0.wireOp",EDGE,"E50.MirrorCS"),sQuery(id+"F0.wireOp",EDGE,"E51.MirrorCS"),sQuery(id+"F0.wireOp",EDGE,"E53.MirrorCS"),sQuery(id+"F0.wireOp",EDGE,"E54.MirrorCS"),sQuery(id+"F0.wireOp",EDGE,"E55.MirrorCS")])],"isStart":false});
            var sketch = newSketch(context, id + "F2", { "sketchPlane" : qUnion([Q0])});
            skLineSegment(sketch, "E56", {"start": v(-11.56, 27.84) * mm, "end": v(-23.94, 73.9) * mm, "construction": true});
            skArc(sketch, "E57", {"start": v(-14.6, 27.02) * mm, "mid": v(-10.74, 24.8) * mm, "end": v(-8.51, 28.66) * mm});
            skArc(sketch, "E58", {"start": v(-15.3, 29.63) * mm, "mid": v(-13.08, 33.5) * mm, "end": v(-9.22, 31.27) * mm});
            skLineSegment(sketch, "E59", {"start": v(-8.51, 28.66) * mm, "end": v(-9.22, 31.27) * mm});
            skLineSegment(sketch, "E60", {"start": v(-15.3, 29.63) * mm, "end": v(-14.6, 27.02) * mm});
            skArc(sketch, "E61", {"start": v(-26.99, 73.09) * mm, "mid": v(-24.76, 76.95) * mm, "end": v(-20.9, 74.72) * mm});
            skArc(sketch, "E62", {"start": v(-26.29, 70.48) * mm, "mid": v(-22.43, 68.26) * mm, "end": v(-20.2, 72.12) * mm});
            skLineSegment(sketch, "E63", {"start": v(-20.9, 74.72) * mm, "end": v(-20.2, 72.12) * mm});
            skLineSegment(sketch, "E64", {"start": v(-26.29, 70.48) * mm, "end": v(-26.99, 73.09) * mm});
            skLineSegment(sketch, "E65.0", {"start": v(-26.99, 73.09) * mm, "end": v(-23.94, 73.9) * mm, "construction": true});
            skLineSegment(sketch, "E66.0", {"start": v(-14.6, 27.02) * mm, "end": v(-8.51, 28.66) * mm, "construction": true});
            skLineSegment(sketch, "E67.0", {"start": v(-8.51, 28.66) * mm, "end": v(-9.22, 31.27) * mm, "construction": true});
            skSolve(sketch);
        }
        {
            var Q0;
            Q0 = qSketchRegion(id + "F2", true);
            extrude(context, id + "F3", {"entities" : qUnion([Q0]), "operationType" : NewBodyOperationType.REMOVE, "endBound" : BoundingType.THROUGH_ALL, "oppositeDirection" : true, "depth" : 25 * mm});
        }
    });
